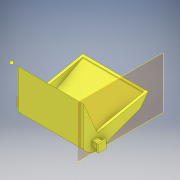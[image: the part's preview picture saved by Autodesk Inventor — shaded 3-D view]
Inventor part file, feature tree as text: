
AUTODESK INVENTOR PART (.ipt)
format: ipt  version: 2018 (Build 220112000, 112)  size: 165,888 bytes
history: native  units: mm
features: sketch x8, extrude x6, projected_geometry x2, plane x1
ambient origin geometry x8: Origin, YZ Plane, XZ Plane, XY Plane, X Axis, Y Axis, Z Axis, Center Point
bodies: Solid1 (feature_tree)
feature tree (17):
  extrude  "Extrusion1"  Depth=500.0mm TaperAngle=0.0deg
  plane  "Work Plane1"
  extrude  "Extrusion2"  Depth=250.109742mm
  extrude  "Extrusion3"  Depth=40.0mm
  extrude  "Extrusion4"  Depth=60.0mm
  extrude  "Extrusion5"  Depth=50.0mm TaperAngle=0.0deg
  sketch  "Sketch6"  dims[d18=60.0mm d19=60.0mm]
  sketch  "Sketch7"  dims[d20=10.0mm]
  extrude  "Extrusion6"  Depth=60.0mm
  sketch  "Sketch1"  dims[d5=300.0mm d6=500.0mm d7=0.0mm]
  sketch  "Sketch2"  dims[d8=-20.0mm d9=250.109742mm]
  sketch  "Sketch3"  dims[d10=460.0mm d11=0.0mm d12=40.0mm]
  sketch  "Sketch4"  dims[d13=40.0mm d14=60.0mm]
  projected_geometry  "Projected Loop1"
  sketch  "Sketch5"  dims[d15=90.0mm d16=50.0mm d17=0.0mm]
  sketch  "Sketch8"  dims[d21=10.0mm d22=10.0mm d23=0.0mm d24=40.0mm d25=40.0mm d26=90.0mm d27=60.0mm d28=50.0mm d29=0.0mm d30=60.0mm d31=60.0mm d33=10.0mm d34=10.0mm d35=10.0mm d36=0.0mm]
  projected_geometry  "Projected Loop2"
